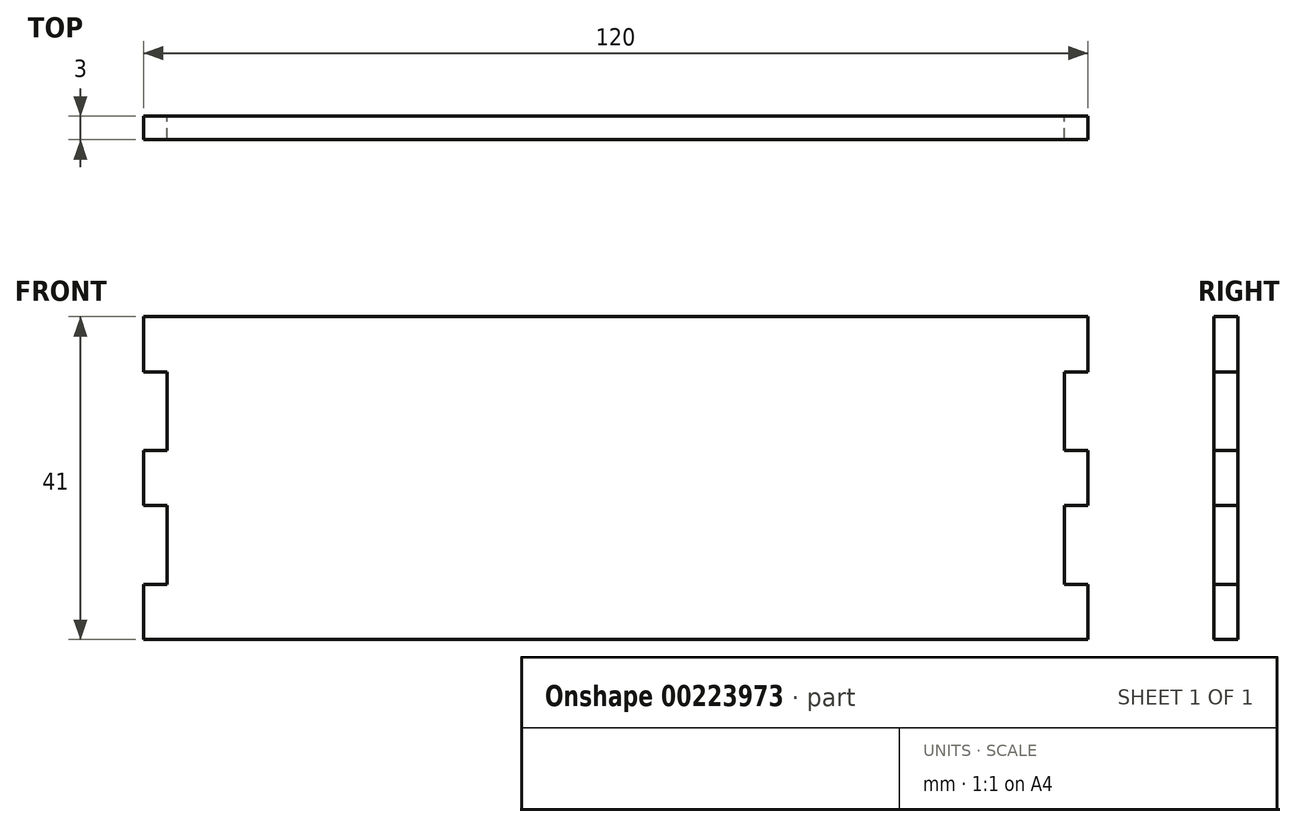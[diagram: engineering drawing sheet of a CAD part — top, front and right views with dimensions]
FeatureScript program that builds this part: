
annotation { "Feature Type Name" : "Feature", "Feature Type Description" : "" }
export const myFeature = defineFeature(function(context is Context, id is Id, definition is map)
    precondition{}
    {
        {
            var Q0;
            Q0=qCreatedBy(makeId("Front.planeOp"),FACE);
            var sketch = newSketch(context, id + "F0", { "sketchPlane" : qUnion([Q0])});
            skLineSegment(sketch, "E0", {"start": v(0, 41) * mm, "end": v(60, 41) * mm});
            skLineSegment(sketch, "E1", {"start": v(60, 41) * mm, "end": v(60, 0) * mm, "construction": true});
            skLineSegment(sketch, "E2", {"start": v(60, 0) * mm, "end": v(0, 0) * mm});
            skLineSegment(sketch, "E3", {"start": v(0, 0) * mm, "end": v(0, 7) * mm});
            skLineSegment(sketch, "E4", {"start": v(0, 7) * mm, "end": v(3, 7) * mm});
            skLineSegment(sketch, "E5", {"start": v(3, 7) * mm, "end": v(3, 17) * mm});
            skLineSegment(sketch, "E6", {"start": v(3, 17) * mm, "end": v(0, 17) * mm});
            skLineSegment(sketch, "E7", {"start": v(0, 17) * mm, "end": v(0, 24) * mm});
            skLineSegment(sketch, "E8", {"start": v(0, 24) * mm, "end": v(3, 24) * mm});
            skLineSegment(sketch, "E9", {"start": v(3, 24) * mm, "end": v(3, 34) * mm});
            skLineSegment(sketch, "E10", {"start": v(3, 34) * mm, "end": v(0, 34) * mm});
            skLineSegment(sketch, "E11", {"start": v(0, 34) * mm, "end": v(0, 41) * mm});
            skLineSegment(sketch, "E12.MirrorCS", {"start": v(120, 7) * mm, "end": v(117, 7) * mm});
            skLineSegment(sketch, "E13.MirrorCS", {"start": v(117, 17) * mm, "end": v(120, 17) * mm});
            skLineSegment(sketch, "E14.MirrorCS", {"start": v(120, 24) * mm, "end": v(117, 24) * mm});
            skLineSegment(sketch, "E15.MirrorCS", {"start": v(117, 34) * mm, "end": v(120, 34) * mm});
            skLineSegment(sketch, "E16.MirrorCS", {"start": v(120, 41) * mm, "end": v(60, 41) * mm});
            skLineSegment(sketch, "E17.MirrorCS", {"start": v(60, 0) * mm, "end": v(120, 0) * mm});
            skLineSegment(sketch, "E18.MirrorCS", {"start": v(120, 0) * mm, "end": v(120, 7) * mm});
            skLineSegment(sketch, "E19.MirrorCS", {"start": v(117, 7) * mm, "end": v(117, 17) * mm});
            skLineSegment(sketch, "E20.MirrorCS", {"start": v(120, 17) * mm, "end": v(120, 24) * mm});
            skLineSegment(sketch, "E21.MirrorCS", {"start": v(117, 24) * mm, "end": v(117, 34) * mm});
            skLineSegment(sketch, "E22.MirrorCS", {"start": v(120, 34) * mm, "end": v(120, 41) * mm});
            skSolve(sketch);
        }
        {
            var Q0;
            Q0 = qSketchRegion(id + "F0", true);
            extrude(context, id + "F1", {"entities" : qUnion([Q0]), "depth" : 3 * mm});
        }
    });
